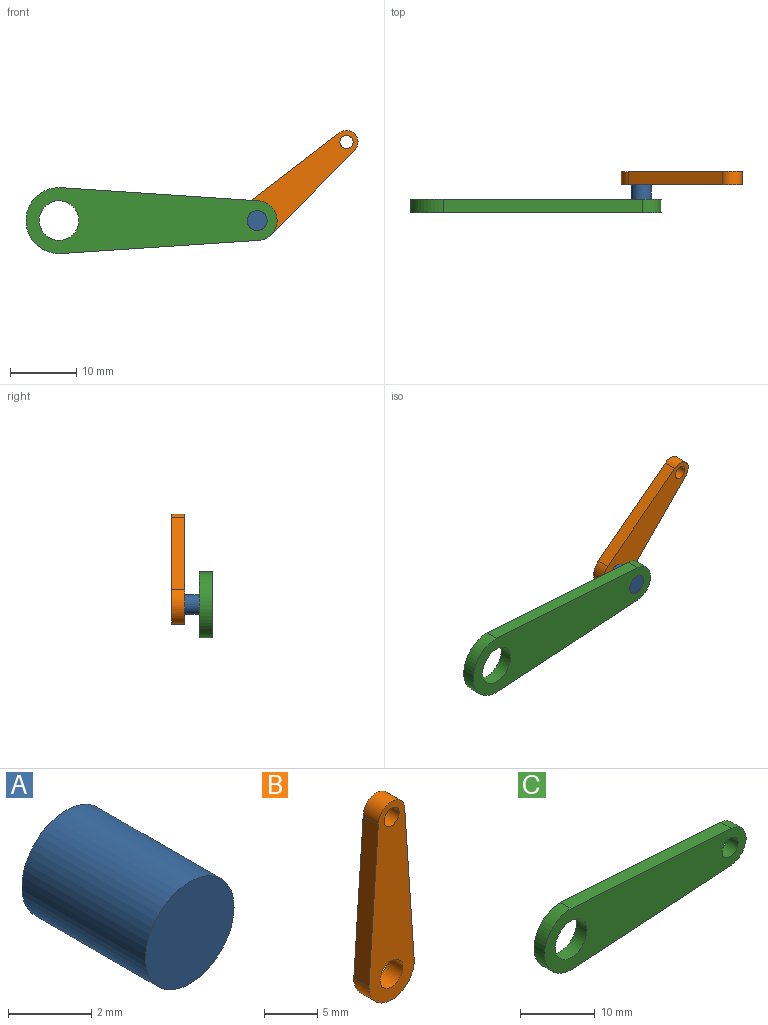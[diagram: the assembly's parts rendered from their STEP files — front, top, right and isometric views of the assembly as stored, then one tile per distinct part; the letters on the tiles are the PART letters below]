
ASSEMBLY  parts=3 mates=2
PART A: 3 faces, bbox 3x4.2x3 mm
  f0: cylinder r=1.5mm len=4.2mm, axis (0,-1,0), area 39.6mm2, adj f1,f2
  f1: plane 3x3mm, normal (0,1,0), area 7.1mm2, adj f0
  f2: plane 3x3mm, normal (0,-1,0), area 7.1mm2, adj f0
PART B: 8 faces, bbox 6x2x22.8 mm
  f0: plane 18x2mm, normal (-1,0,0.07), area 36.1mm2, adj f1,f4,f6,f7
  f1: cylinder r=3mm len=6mm, axis (0,-1,0), area 18.8mm2, adj f0,f2,f6,f7
  f2: plane 18x2mm, normal (1,0,0.07), area 36.1mm2, adj f1,f4,f6,f7
  f3: cylinder r=1mm len=2mm, axis (0,-1,0), area 12.6mm2, adj f6,f7
  f4: cylinder r=1.75mm len=3.5mm, axis (0,-1,0), area 11mm2, adj f0,f2,f6,f7
  f5: cylinder r=1.5mm len=3mm, axis (0,-1,0), area 18.8mm2, adj f6,f7
  f6: plane 22.75x6mm, normal (0,1,0), area 94.2mm2, adj f0,f1,f2,f3,f4,f5
  f7: plane 22.75x6mm, normal (0,-1,0), area 94.2mm2, adj f0,f1,f2,f3,f4,f5
PART C: 8 faces, bbox 38x2x10 mm
  f0: plane 30.2x2.01mm, normal (0.07,0,1), area 60.5mm2, adj f1,f4,f6,f7
  f1: cylinder r=5mm len=10mm, axis (0,1,0), area 31.4mm2, adj f0,f2,f6,f7
  f2: plane 30.2x2.01mm, normal (0.07,0,-1), area 60.5mm2, adj f1,f4,f6,f7
  f3: cylinder r=1.5mm len=3mm, axis (0,1,0), area 18.8mm2, adj f6,f7
  f4: cylinder r=3mm len=5.99mm, axis (0,1,0), area 18.1mm2, adj f0,f2,f6,f7
  f5: cylinder r=3mm len=6mm, axis (0,1,0), area 37.7mm2, adj f6,f7
  f6: plane 38x10mm, normal (0,-1,0), area 258.3mm2, adj f0,f1,f2,f3,f4,f5
  f7: plane 38x10mm, normal (0,1,0), area 258.3mm2, adj f0,f1,f2,f3,f4,f5
PLACE A rot(axis=(0,1,0),39.6deg) t=(-8.36,-0.2,12.76)mm
PLACE B rot(axis=(-0.41,0,-0.91),180deg) t=(16.69,3.9,-11.53)mm
PLACE C t=(-12.4,-0.3,1.6)mm fixed
MATE revolute A.f0 <-> B.f1  axis (0,1,0) through (5.12,1.9,1.6)mm
MATE revolute A.f0 <-> C.f3  axis (0,-1,0) through (5.12,-2.3,1.6)mm
